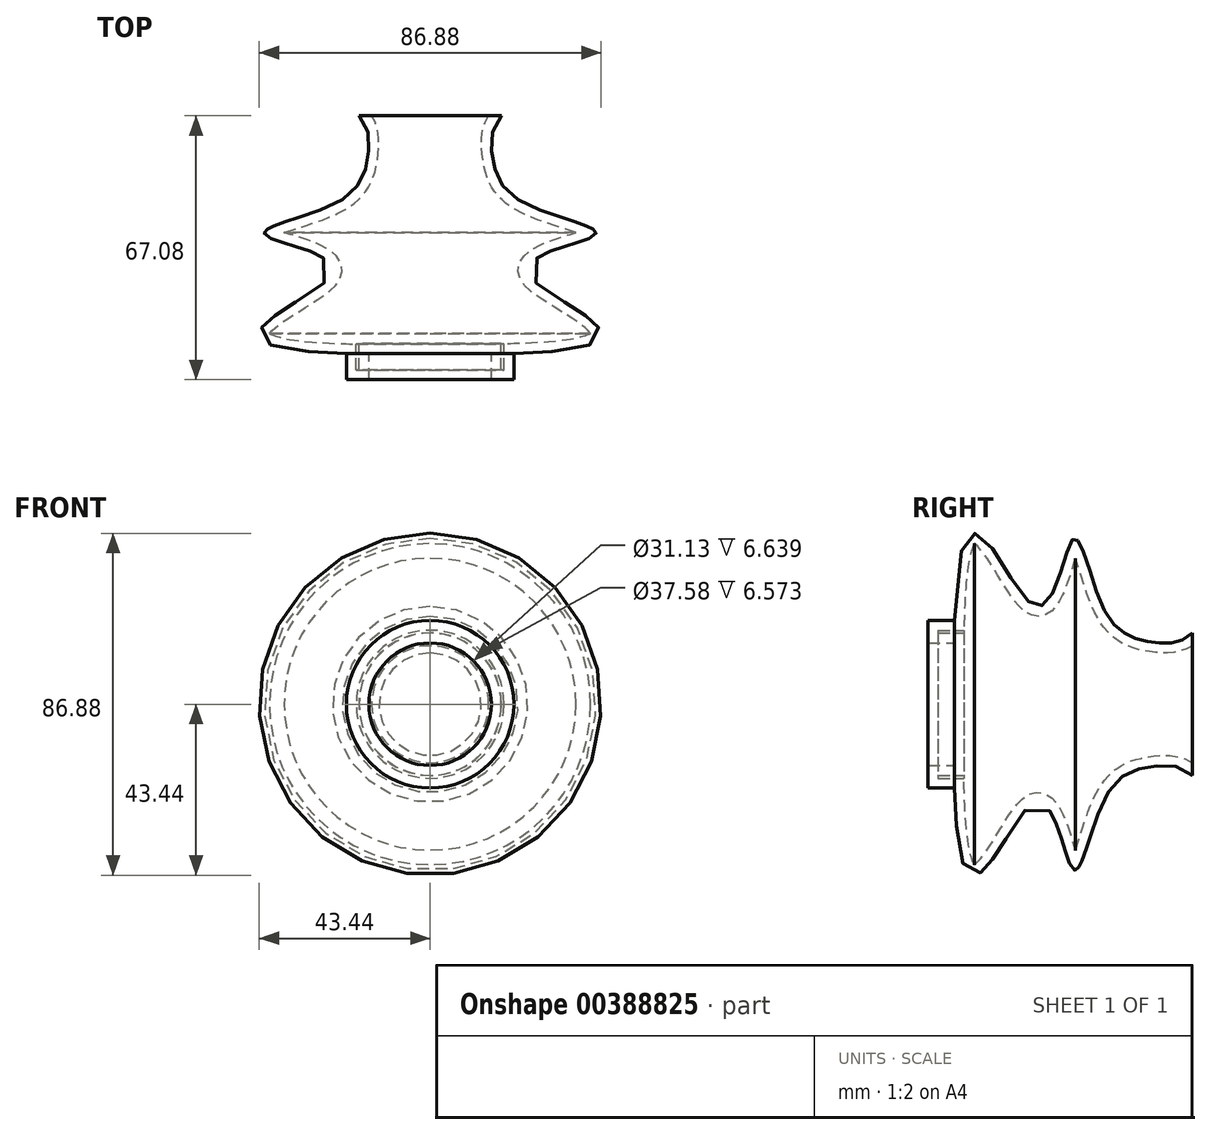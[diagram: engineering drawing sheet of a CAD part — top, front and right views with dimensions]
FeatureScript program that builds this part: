
annotation { "Feature Type Name" : "Feature", "Feature Type Description" : "" }
export const myFeature = defineFeature(function(context is Context, id is Id, definition is map)
    precondition{}
    {
        {
            var Q0;
            Q0=qCreatedBy(makeId("Top.planeOp"),FACE);
            var sketch = newSketch(context, id + "F0", { "sketchPlane" : qUnion([Q0])});
            skLineSegment(sketch, "E0", {"start": v(0, 46.93) * mm, "end": v(0, -13.5) * mm});
            skLineSegment(sketch, "E1", {"start": v(0, -13.5) * mm, "end": v(15.57, -13.5) * mm});
            skLineSegment(sketch, "E2", {"start": v(15.57, -13.5) * mm, "end": v(15.57, -20.15) * mm});
            skLineSegment(sketch, "E3", {"start": v(15.57, -20.15) * mm, "end": v(21.29, -20.15) * mm});
            skLineSegment(sketch, "E4", {"start": v(21.29, -20.15) * mm, "end": v(21.29, -13.5) * mm});
            skLineSegment(sketch, "E5", {"start": v(0, 46.93) * mm, "end": v(18.1, 46.93) * mm});
            skFitSpline(sketch, "E6", {"points": [v(18.1, 46.93) * mm, v(15.84, 36.3) * mm, v(23.83, 24.7) * mm, v(41.76, 16.45) * mm, v(26.12, 5.2) * mm, v(21.29, -13.5) * mm], "startDerivative": vector(-54.26, -51.8) * mm, "endDerivative": vector(-596.03, -15.86) * mm});
            skSolve(sketch);
        }
        {
            var Q0;
            Q0=makeQuery(id+"F0.imprint","IMPRINT",FACE,{"disambiguationData":[TD([[makeQuery(id+"F0.imprint","IMPRINT",EDGE,{"derivedFrom":sQuery(id+"F0.wireOp",EDGE,"E0")}),1.0]])]});
            var Q1;
            Q1=sQuery(id+"F0.wireOp",EDGE,"E0");
            revolve(context, id + "F1", {"entities" : qUnion([Q0]), "axis" : qUnion([Q1]), "revolveType" : RevolveType.FULL});
        }
        {
            var Q0;
            Q0=makeQuery(id+"F1.opRevolve","SWEPT_FACE",FACE,{"disambiguationData":[OSD([sQuery(id+"F0.wireOp",EDGE,"E5")])]});
            shell(context, id + "F2", {"entities" : qUnion([Q0]), "thickness" : 2.5 * mm});
        }
    });
